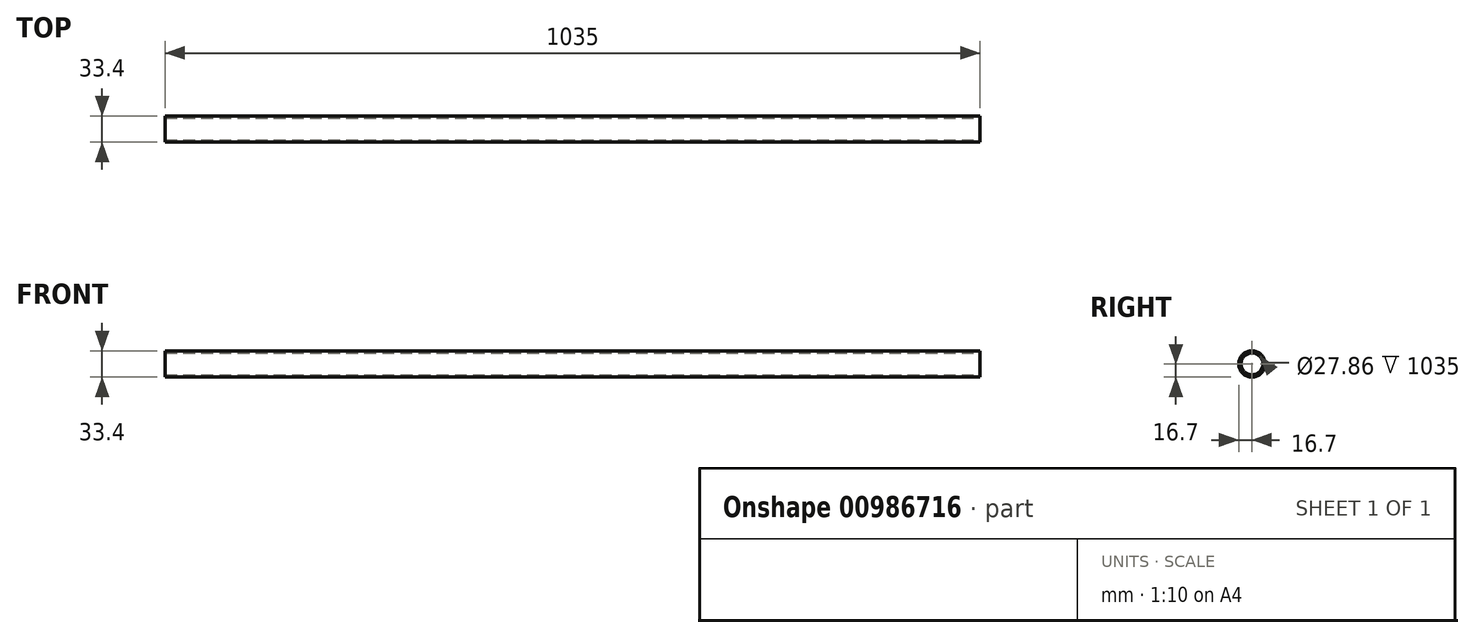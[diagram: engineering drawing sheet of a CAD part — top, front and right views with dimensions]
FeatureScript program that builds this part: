
annotation { "Feature Type Name" : "Feature", "Feature Type Description" : "" }
export const myFeature = defineFeature(function(context is Context, id is Id, definition is map)
    precondition{}
    {
        {
            var Q0;
            Q0=qCreatedBy(makeId("Front.planeOp"),FACE);
            var sketch = newSketch(context, id + "F0", { "sketchPlane" : qUnion([Q0])});
            skLineSegment(sketch, "E0", {"start": v(0, 0) * mm, "end": v(1035, 0) * mm});
            skSolve(sketch);
        }
        {
            var Q0;
            Q0=qCreatedBy(makeId("Right.planeOp"),FACE);
            var sketch = newSketch(context, id + "F1", { "sketchPlane" : qUnion([Q0])});
            skCircle(sketch, "E1", {"center": v(0, 0) * mm, "radius": 16.7 * mm});
            skCircle(sketch, "E2.0", {"center": v(0, 0) * mm, "radius": 13.93 * mm});
            skSolve(sketch);
        }
        {
            var Q0;
            Q0=makeQuery(id+"F1.imprint","IMPRINT",FACE,{"disambiguationData":[TD([[makeQuery(id+"F1.imprint","IMPRINT",EDGE,{"derivedFrom":sQuery(id+"F1.wireOp",EDGE,"E1")}),1.0]])]});
            var Q1;
            Q1=sQuery(id+"F0.wireOp",EDGE,"E0");
            sweep(context, id + "F2", {"profiles" : qUnion([Q0]), "path" : qUnion([Q1])});
        }
    });
